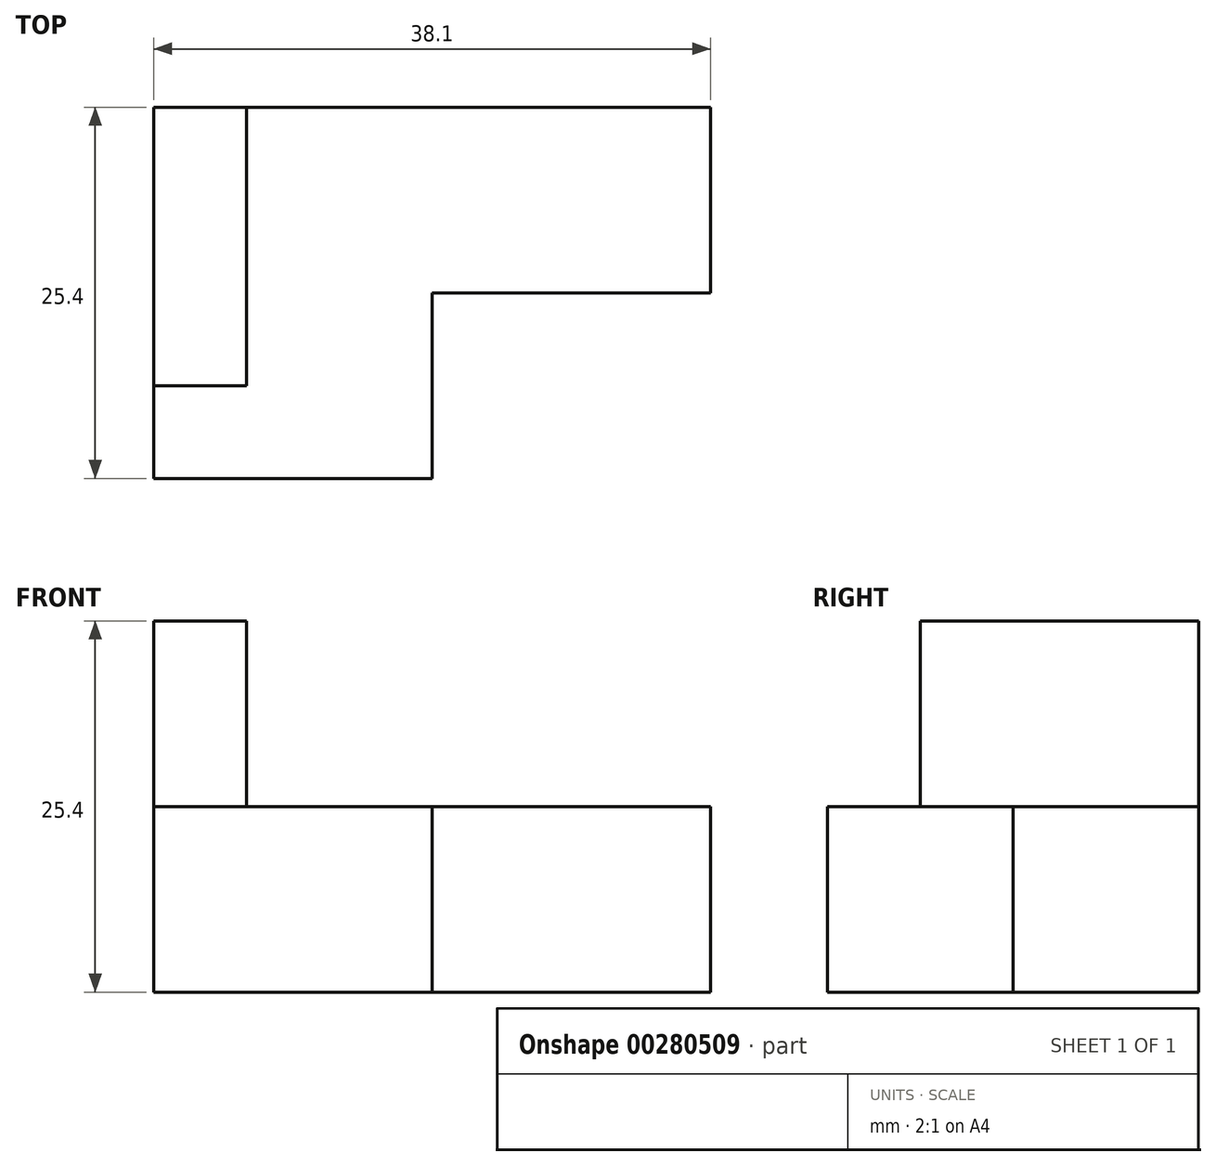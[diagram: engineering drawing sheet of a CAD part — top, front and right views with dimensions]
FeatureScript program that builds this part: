
annotation { "Feature Type Name" : "Feature", "Feature Type Description" : "" }
export const myFeature = defineFeature(function(context is Context, id is Id, definition is map)
    precondition{}
    {
        {
            var Q0;
            Q0=qCreatedBy(makeId("Front.planeOp"),FACE);
            var sketch = newSketch(context, id + "F0", { "sketchPlane" : qUnion([Q0])});
            skLineSegment(sketch, "E0", {"start": v(0, 0) * mm, "end": v(38.1, 0) * mm});
            skLineSegment(sketch, "E1", {"start": v(0, 0) * mm, "end": v(0, 12.7) * mm});
            skLineSegment(sketch, "E2", {"start": v(0, 12.7) * mm, "end": v(38.1, 12.7) * mm});
            skLineSegment(sketch, "E3", {"start": v(38.1, 12.7) * mm, "end": v(38.1, 0) * mm});
            skSolve(sketch);
        }
        {
            var Q0;
            Q0=makeQuery(id+"F0.imprint","IMPRINT",FACE,{"disambiguationData":[TD([[makeQuery(id+"F0.imprint","IMPRINT",EDGE,{"derivedFrom":sQuery(id+"F0.wireOp",EDGE,"E0")}),1.0]])]});
            extrude(context, id + "F1", {"entities" : qUnion([Q0]), "depth" : 25.4 * mm});
        }
        {
            var Q0;
            Q0=makeQuery(id+"F1.opExtrude","CAP_FACE",FACE,{"disambiguationData":[OSD([sQuery(id+"F0.wireOp",EDGE,"E0"),sQuery(id+"F0.wireOp",EDGE,"E1"),sQuery(id+"F0.wireOp",EDGE,"E2"),sQuery(id+"F0.wireOp",EDGE,"E3")])],"isStart":false});
            var sketch = newSketch(context, id + "F2", { "sketchPlane" : qUnion([Q0])});
            skLineSegment(sketch, "E4.bottom", {"start": v(19.05, 12.7) * mm, "end": v(38.1, 12.7) * mm});
            skLineSegment(sketch, "E4.top", {"start": v(19.05, 0) * mm, "end": v(38.1, 0) * mm});
            skLineSegment(sketch, "E4.left", {"start": v(19.05, 12.7) * mm, "end": v(19.05, 0) * mm});
            skLineSegment(sketch, "E4.right", {"start": v(38.1, 12.7) * mm, "end": v(38.1, 0) * mm});
            skSolve(sketch);
        }
        {
            var Q0;
            Q0=makeQuery(id+"F2.imprint","IMPRINT",FACE,{"disambiguationData":[TD([[makeQuery(id+"F2.imprint","IMPRINT",EDGE,{"derivedFrom":sQuery(id+"F2.wireOp",EDGE,"E4.bottom")}),-1.0]])]});
            extrude(context, id + "F3", {"entities" : qUnion([Q0]), "operationType" : NewBodyOperationType.REMOVE, "oppositeDirection" : true, "depth" : 12.7 * mm});
        }
        {
            var Q0;
            Q0=makeQuery(id+"F1.opExtrude","SWEPT_FACE",FACE,{"disambiguationData":[OSD([sQuery(id+"F0.wireOp",EDGE,"E2")])]});
            var sketch = newSketch(context, id + "F4", { "sketchPlane" : qUnion([Q0])});
            skLineSegment(sketch, "E5.bottom", {"start": v(0, 0) * mm, "end": v(6.35, 0) * mm});
            skLineSegment(sketch, "E5.top", {"start": v(0, -19.05) * mm, "end": v(6.35, -19.05) * mm});
            skLineSegment(sketch, "E5.left", {"start": v(0, 0) * mm, "end": v(0, -19.05) * mm});
            skLineSegment(sketch, "E5.right", {"start": v(6.35, 0) * mm, "end": v(6.35, -19.05) * mm});
            skSolve(sketch);
        }
        {
            var Q0;
            Q0=makeQuery(id+"F4.imprint","IMPRINT",FACE,{"disambiguationData":[TD([[makeQuery(id+"F4.imprint","IMPRINT",EDGE,{"derivedFrom":sQuery(id+"F4.wireOp",EDGE,"E5.bottom")}),-1.0]])]});
            extrude(context, id + "F5", {"entities" : qUnion([Q0]), "operationType" : NewBodyOperationType.ADD, "depth" : 12.7 * mm});
        }
    });
